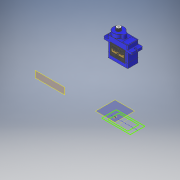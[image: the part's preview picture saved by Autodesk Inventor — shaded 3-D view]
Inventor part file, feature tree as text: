
AUTODESK INVENTOR PART (.ipt)
format: ipt  version: 2019 (Build 230136000, 136)  size: 1,570,816 bytes
history: native  units: in
note: dims shown in document units (in); Inventor stores cm internally (conversion verified against a paired STEP export)
features: other x13, plane x2, sketch x2
ambient origin geometry x8: Origin, YZ Plane, XZ Plane, XY Plane, X Axis, Y Axis, Z Axis, Center Point
bodies: Solid1 (feature_tree), Solid2 (feature_tree), Solid3 (feature_tree), Solid4 (feature_tree), Solid5 (feature_tree), Solid6 (feature_tree), Solid7 (feature_tree), Solid8 (feature_tree), Solid9 (feature_tree), Solid10 (feature_tree), Solid11 (feature_tree), Solid12 (feature_tree), Solid13 (feature_tree)
feature tree (17):
  plane  "Work Plane1"
  sketch  "Sketch1"  dims[d0=3.0in]
  plane  "Work Plane3"
  sketch  "Sketch6"
  other  "SG90 - Micro Servo 9g - Tower Pro.1-1-solid1"
  other  "SG90 - Micro Servo 9g - Tower Pro.1-1-solid2"
  other  "SG90 - Micro Servo 9g - Tower Pro.1-1-solid3"
  other  "SG90 - Micro Servo 9g - Tower Pro.1-1-solid4"
  other  "SG90 - Micro Servo 9g - Tower Pro.1-1-solid5"
  other  "SG90 - Micro Servo 9g - Tower Pro.1-1-solid6"
  other  "SG90 - Micro Servo 9g - Tower Pro.1-1-solid7"
  other  "SG90 - Micro Servo 9g - Tower Pro.1-1-solid8"
  other  "SG90 - Micro Servo 9g - Tower Pro.1-1-solid9"
  other  "SG90 - Micro Servo 9g - Tower Pro.1-1-solid10"
  other  "SG90 - Micro Servo 9g - Tower Pro.1-1-solid11"
  other  "SG90 - Micro Servo 9g - Tower Pro.1-1-solid12"
  other  "SG90 - Micro Servo 9g - Tower Pro.1-1-solid13"
